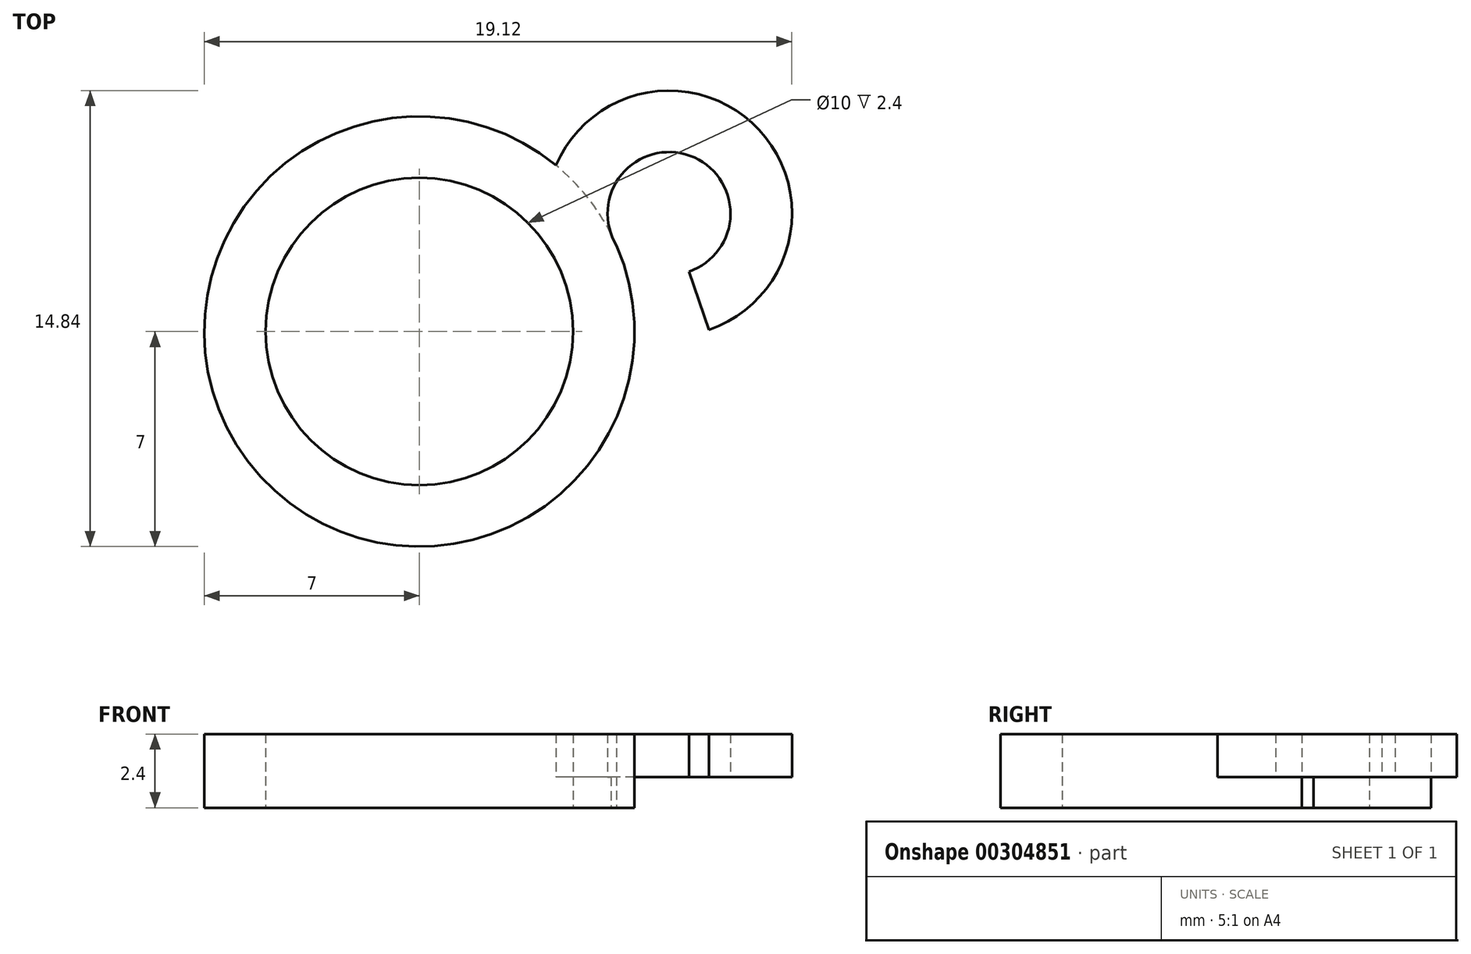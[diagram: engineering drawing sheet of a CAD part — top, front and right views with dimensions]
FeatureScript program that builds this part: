
annotation { "Feature Type Name" : "Feature", "Feature Type Description" : "" }
export const myFeature = defineFeature(function(context is Context, id is Id, definition is map)
    precondition{}
    {
        {
            var Q0;
            Q0=qCreatedBy(makeId("Top.planeOp"),FACE);
            var sketch = newSketch(context, id + "F0", { "sketchPlane" : qUnion([Q0])});
            skCircle(sketch, "E0", {"center": v(0, 0) * mm, "radius": 7 * mm});
            skCircle(sketch, "E1", {"center": v(0, 0) * mm, "radius": 5 * mm});
            skCircle(sketch, "E2", {"center": v(8.12, 3.84) * mm, "radius": 4 * mm});
            skPoint(sketch, "E2.first.point", {"position": v(7, 0) * mm});
            skPoint(sketch, "E2.second.point", {"position": v(11.72, 5.58) * mm});
            skPoint(sketch, "E2.third.point", {"position": v(4.62, 1.9) * mm});
            skCircle(sketch, "E3.0", {"center": v(8.12, 3.84) * mm, "radius": 2 * mm});
            skLineSegment(sketch, "E4", {"start": v(8.12, 3.84) * mm, "end": v(9.42, 0.05) * mm});
            skLineSegment(sketch, "E5", {"start": v(8.12, 3.84) * mm, "end": v(4.62, 1.9) * mm});
            skSolve(sketch);
        }
        {
            var Q0;
            {var subQ0=sQuery(id+"F0.wireOp",EDGE,"E2");var subQ1=sQuery(id+"F0.wireOp",EDGE,"E0");var subQ2=makeQuery(id+"F0.imprint","INTERSECT",VERTEX,{"disambiguationData":[OD(1.0)],"derivedFrom":[subQ1,subQ0]});Q0=makeQuery(id+"F0.imprint","IMPRINT",FACE,{"disambiguationData":[TD([[makeQuery(id+"F0.imprint","IMPRINT",EDGE,{"disambiguationData":[TD([[subQ2,1.0]])],"derivedFrom":subQ1}),1.0]])]});}
            var Q1;
            {var subQ1=sQuery(id+"F0.wireOp",EDGE,"E2");var subQ5=sQuery(id+"F0.wireOp",EDGE,"E0");var subQ6=makeQuery(id+"F0.imprint","INTERSECT",VERTEX,{"disambiguationData":[OD(1.0)],"derivedFrom":[subQ5,subQ1]});Q1=makeQuery(id+"F0.imprint","IMPRINT",FACE,{"disambiguationData":[TD([[makeQuery(id+"F0.imprint","IMPRINT",EDGE,{"disambiguationData":[TD([[subQ6,1.0]])],"derivedFrom":subQ5}),-1.0]])]});}
            var Q2;
            {var subQ0=sQuery(id+"F0.wireOp",EDGE,"E2");var subQ1=sQuery(id+"F0.wireOp",EDGE,"E0");var subQ2=makeQuery(id+"F0.imprint","INTERSECT",VERTEX,{"disambiguationData":[OD(0.0)],"derivedFrom":[subQ1,subQ0]});Q2=makeQuery(id+"F0.imprint","IMPRINT",FACE,{"disambiguationData":[TD([[makeQuery(id+"F0.imprint","IMPRINT",EDGE,{"disambiguationData":[TD([[subQ2,1.0]])],"derivedFrom":subQ1}),1.0]])]});}
            var Q3;
            {var subQ0=sQuery(id+"F0.wireOp",EDGE,"E2");var subQ1=sQuery(id+"F0.wireOp",EDGE,"E0");var subQ2=makeQuery(id+"F0.imprint","INTERSECT",VERTEX,{"disambiguationData":[OD(0.0)],"derivedFrom":[subQ1,subQ0]});Q3=makeQuery(id+"F0.imprint","IMPRINT",FACE,{"disambiguationData":[TD([[makeQuery(id+"F0.imprint","IMPRINT",EDGE,{"disambiguationData":[TD([[subQ2,-1.0]])],"derivedFrom":subQ1}),1.0]])]});}
            extrude(context, id + "F1", {"entities" : qUnion([Q0, Q1, Q2, Q3]), "depth" : 2.4 * mm});
        }
        {
            var Q0;
            {var subQ0=sQuery(id+"F0.wireOp",EDGE,"E2");var subQ1=sQuery(id+"F0.wireOp",EDGE,"E0");var subQ2=makeQuery(id+"F0.imprint","INTERSECT",VERTEX,{"disambiguationData":[OD(1.0)],"derivedFrom":[subQ1,subQ0]});Q0=makeQuery(id+"F0.imprint","IMPRINT",FACE,{"disambiguationData":[TD([[makeQuery(id+"F0.imprint","IMPRINT",EDGE,{"disambiguationData":[TD([[subQ2,1.0]])],"derivedFrom":subQ1}),-1.0]])]});}
            extrude(context, id + "F2", {"entities" : qUnion([Q0]), "operationType" : NewBodyOperationType.REMOVE, "depth" : 1 * mm});
        }
    });
